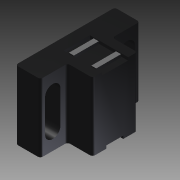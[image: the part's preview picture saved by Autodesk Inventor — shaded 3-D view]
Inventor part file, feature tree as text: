
AUTODESK INVENTOR PART (.ipt)
format: ipt  version: 2016 (Build 200138000, 138)  size: 166,400 bytes
history: native  units: mm
features: extrude x8, sketch x8, other x7
ambient origin geometry x8: Origin, YZ Plane, XZ Plane, XY Plane, X Axis, Y Axis, Z Axis, Center Point
bodies: Solid1 (feature_tree)
feature tree (23):
  extrude  "Extrusion1"  Depth=10.0mm TaperAngle=0.0deg
  extrude  "Extrusion2"  Depth=15.32mm TaperAngle=0.0deg
  extrude  "Extrusion3"  Depth=10.0mm TaperAngle=0.0deg
  extrude  "Extrusion4"  Depth=6.0mm TaperAngle=0.0deg
  extrude  "Extrusion5"  [1 undecoded]
  extrude  "Extrusion6"  [1 undecoded]
  extrude  "Extrusion7"  [1 undecoded]
  extrude  "Extrusion8"  [1 undecoded]
  other  "side_1_XY"
  other  "side_1_YZ"
  other  "side_1_ZX"
  other  "side_1_X"
  other  "side_1_Y"
  other  "side_1_Z"
  other  "side_1_Center"
  sketch  "Skizze_1"  dims[d0=27.5mm d1=0.0mm d2=10.0mm d3=0.0mm]
  sketch  "Skizze_2"  dims[d4=10.0mm d5=0.0mm d6=15.32mm d7=0.0mm]
  sketch  "Skizze_3"  dims[d8=15.32mm d9=0.0mm d10=10.0mm d11=0.0mm]
  sketch  "Skizze_4"  dims[d12=6.75mm d13=0.0mm d14=6.0mm d15=0.0mm]
  sketch  "Skizze_5"
  sketch  "Skizze_6"
  sketch  "Skizze_7"
  sketch  "Skizze_8"
note: 4 required parameter values undecoded (feature->parameter linkage not recoverable at this tier; creation-order binding heuristic only, values carry confidence <= 0.55)
